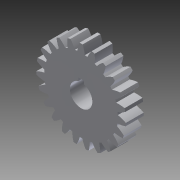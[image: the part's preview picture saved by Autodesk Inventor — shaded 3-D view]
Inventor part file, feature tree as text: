
AUTODESK INVENTOR PART (.ipt)
format: ipt  version: 2014 SP1 (Build 180222100, 222)  size: 222,208 bytes
history: native  units: in
note: dims shown in document units (in); Inventor stores cm internally (conversion verified against a paired STEP export)
features: extrude x1, sketch x1
ambient origin geometry x8: Origin, YZ Plane, XZ Plane, XY Plane, X Axis, Y Axis, Z Axis, Center Point
bodies: Solid1 (feature_tree)
feature tree (2):
  extrude  "Extrusion1"  Depth=0.25in
  sketch  "Sketch1"  dims[d0=0.315in d1=0.0394in d2=0.0394in d3=0.0394in d4=0.25in d5=0.0in]
